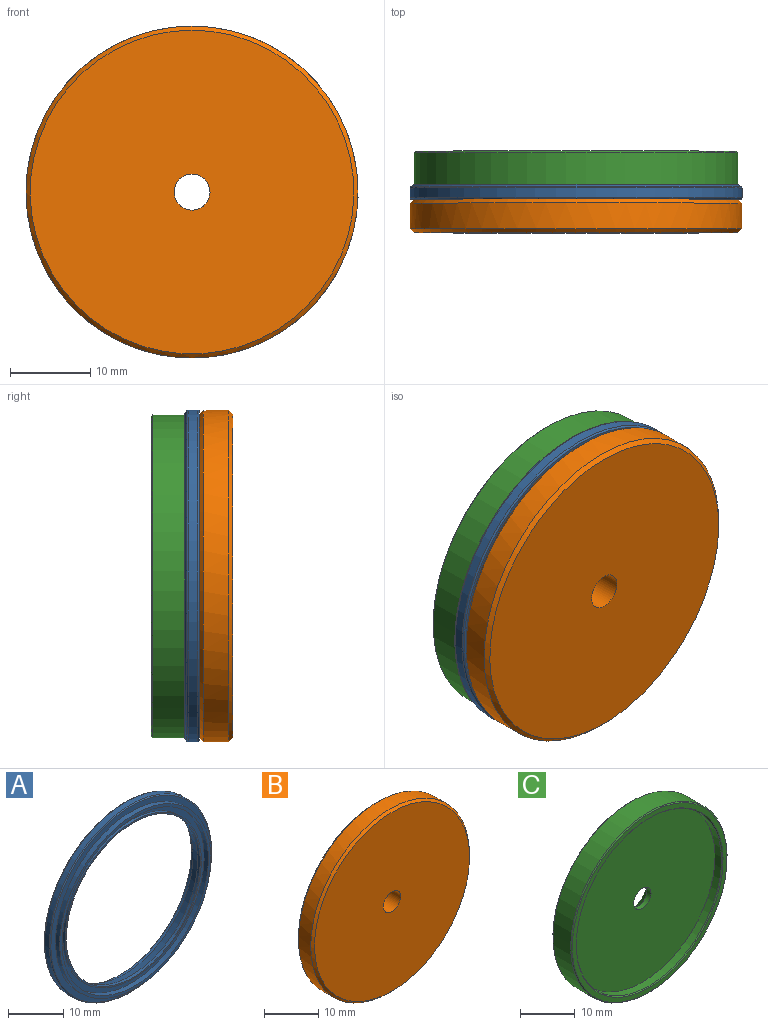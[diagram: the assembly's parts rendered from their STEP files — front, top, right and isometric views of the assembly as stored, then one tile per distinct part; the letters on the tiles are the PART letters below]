
ASSEMBLY  parts=3 mates=2
PART A: 22 faces, bbox 44.9x3.8x44.9 mm
  f0: cylinder r=18.75mm len=37.5mm, axis (0,1,0), area 129.6mm2, adj f1,f21
  f1: plane 38.7x38.7mm, normal (0,-1,0), area 71.8mm2, adj f0,f2
  f2: cylinder r=19.35mm len=38.7mm, axis (0,1,0), area 127.7mm2, adj f1,f3
  f3: plane 41.1x41.1mm, normal (0,-1,0), area 150.4mm2, adj f2,f4
  f4: torus R=20.55mm, axis (0,1,0), area 40.8mm2, adj f3,f5
  f5: cylinder r=20.75mm len=41.5mm, axis (0,1,0), area 155.5mm2, adj f4,f6
  f6: torus R=20.55mm, axis (0,1,0), area 25.6mm2, adj f5,f7
  f7: cone r=20.3mm half-angle=56.3deg, axis (0,-1,0), area 55.4mm2, adj f6,f8
  f8: torus R=20.28mm, axis (0,1,0), area 13.7mm2, adj f7,f9
  f9: cylinder r=20.23mm len=40.45mm, axis (0,1,0), area 96.1mm2, adj f8,f10
  f10: plane 40.45x40.45mm, normal (0,1,0), area 180.6mm2, adj f9,f11
  f11: cylinder r=18.75mm len=37.5mm, axis (0,1,0), area 106mm2, adj f10,f12
  f12: cone r=18.29mm half-angle=28.6deg, axis (0,-1,0), area 112.6mm2, adj f11,f13
  f13: plane 36.57x36.57mm, normal (0,1,0), area 9.9mm2, adj f12,f14
  f14: cylinder r=18.2mm len=36.4mm, axis (0,1,0), area 97.2mm2, adj f13,f15
  f15: cone r=18.2mm half-angle=30deg, axis (0,-1,0), area 19.9mm2, adj f14,f16
  f16: plane 36.57x36.57mm, normal (0,1,0), area 71.9mm2, adj f15,f17
  f17: cone r=17.15mm half-angle=16.9deg, axis (0,1,0), area 188.5mm2, adj f16,f18
  f18: cylinder r=17.15mm len=34.3mm, axis (0,1,0), area 70mm2, adj f17,f19
  f19: plane 34.9x34.9mm, normal (0,-1,0), area 32.6mm2, adj f18,f20
  f20: cylinder r=17.45mm len=34.9mm, axis (0,1,0), area 65.8mm2, adj f19,f21
  f21: plane 37.5x37.5mm, normal (0,-1,0), area 147.8mm2, adj f0,f20
PART B: 10 faces, bbox 41.5x4.2x41.5 mm
  f0: cylinder r=19.35mm len=38.7mm, axis (0,-1,0), area 127.7mm2, adj f1,f6
  f1: plane 38.7x38.7mm, normal (0,1,0), area 80.6mm2, adj f0,f2
  f2: cylinder r=18.68mm len=37.35mm, axis (0,-1,0), area 41.1mm2, adj f1,f3
  f3: plane 37.35x37.35mm, normal (0,1,0), area 1079.7mm2, adj f2,f9
  f4: plane 40.45x40.45mm, normal (0,-1,0), area 1269.2mm2, adj f7,f9
  f5: cylinder r=20.73mm len=41.45mm, axis (0,-1,0), area 416.7mm2, adj f7,f8
  f6: plane 40.45x40.45mm, normal (0,1,0), area 108.8mm2, adj f0,f8
  f7: cone r=20.23mm half-angle=45deg, axis (0,1,0), area 91mm2, adj f4,f5
  f8: cone r=20.73mm half-angle=45deg, axis (0,-1,0), area 91mm2, adj f5,f6
  f9: cylinder r=2.25mm len=4.5mm, axis (0,1,0), area 49.5mm2, adj f3,f4
PART C: 10 faces, bbox 40.5x5x40.5 mm
  f0: plane 37.6x37.6mm, normal (0,-1,0), area 1094.5mm2, adj f1,f7
  f1: cylinder r=18.8mm len=37.6mm, axis (0,-1,0), area 200.2mm2, adj f0,f6
  f2: plane 40.05x40.05mm, normal (0,-1,0), area 125.7mm2, adj f5,f6
  f3: cylinder r=20.23mm len=40.45mm, axis (0,-1,0), area 584.6mm2, adj f5,f9
  f4: plane 40.05x40.05mm, normal (0,1,0), area 1203mm2, adj f8,f9
  f5: cone r=20.03mm half-angle=45deg, axis (0,1,0), area 35.8mm2, adj f2,f3
  f6: cone r=18.8mm half-angle=45deg, axis (0,-1,0), area 33.6mm2, adj f1,f2
  f7: cylinder r=2.25mm len=4.5mm, axis (0,1,0), area 15.6mm2, adj f0,f8
  f8: cone r=2.25mm half-angle=45deg, axis (0,1,0), area 57.8mm2, adj f4,f7
  f9: cone r=20.23mm half-angle=45deg, axis (0,-1,0), area 35.8mm2, adj f3,f4
PLACE A t=(-10.54,-10.66,4.21)mm
PLACE B t=(-8.34,-11.66,4.21)mm fixed
PLACE C t=(-8.89,-10.66,4.21)mm
MATE fastened A.f0 <-> C.f1  axis (0,1,0) through (-27.69,-10.66,4.21)mm
MATE fastened B.f0 <-> A.f0  axis (0,1,0) through (-27.69,-11.66,4.21)mm
